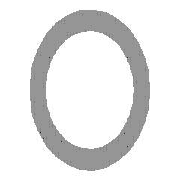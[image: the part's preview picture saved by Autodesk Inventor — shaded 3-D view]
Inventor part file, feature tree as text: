
AUTODESK INVENTOR PART (.ipt)
format: ipt  version: 2025 (Build 290162010, 162A)  size: 125,440 bytes
history: native  units: mm (DEFAULTED — no unit token found)
features: other x3, sketch x1, plane x1
ambient origin geometry x8: Origin, YZ Plane, XZ Plane, XY Plane, X Axis, Y Axis, Z Axis, Center Point
bodies: Solid1 (feature_tree), Body (feature_tree)
feature tree (5):
  other  "Driven Length"
  other  "Start plane"
  other  "End plane"
  sketch  "Sketch3"  dims[d0=168.3mm d1=2.0mm d2=200.0mm d3=0.0mm d4=-0.0mm d5=200.0mm d6=90.0deg d7=200.0mm]
  plane  "Work Plane3"
